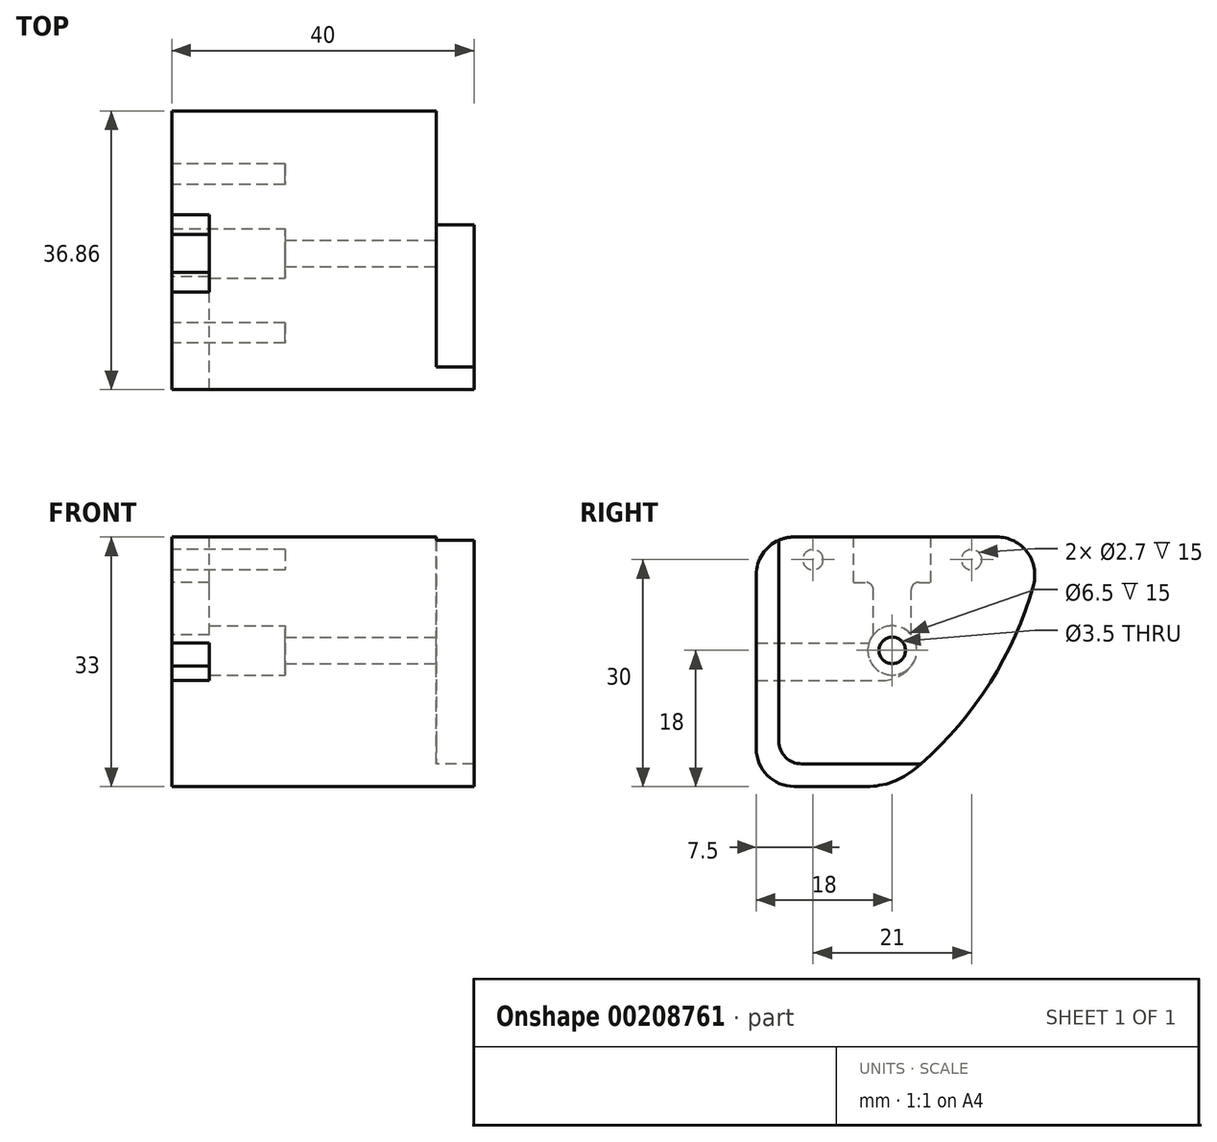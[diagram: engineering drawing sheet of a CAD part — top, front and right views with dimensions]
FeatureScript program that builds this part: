
annotation { "Feature Type Name" : "Feature", "Feature Type Description" : "" }
export const myFeature = defineFeature(function(context is Context, id is Id, definition is map)
    precondition{}
    {
        {
            var Q0;
            Q0=qCreatedBy(makeId("Right.planeOp"),FACE);
            var sketch = newSketch(context, id + "F0", { "sketchPlane" : qUnion([Q0])});
            skLineSegment(sketch, "E0", {"start": v(0, 0) * mm, "end": v(-15, 0) * mm, "construction": true});
            skLineSegment(sketch, "E1", {"start": v(-15, 0) * mm, "end": v(-15, -15) * mm});
            skLineSegment(sketch, "E2", {"start": v(-15, -15) * mm, "end": v(0, -15) * mm});
            skCircle(sketch, "E3", {"center": v(0, 0) * mm, "radius": 1.75 * mm});
            skLineSegment(sketch, "E4", {"start": v(-18, 0) * mm, "end": v(-18, -18) * mm});
            skLineSegment(sketch, "E5", {"start": v(-18, -18) * mm, "end": v(0, -18) * mm});
            skLineSegment(sketch, "E6", {"start": v(0, -18) * mm, "end": v(20, -18) * mm});
            skLineSegment(sketch, "E7", {"start": v(-18, 0) * mm, "end": v(-18, 15) * mm});
            skLineSegment(sketch, "E8", {"start": v(-18, 15) * mm, "end": v(20, 15) * mm});
            skLineSegment(sketch, "E9", {"start": v(20, 15) * mm, "end": v(20, -18) * mm});
            skLineSegment(sketch, "E10", {"start": v(0, -15) * mm, "end": v(0, -18) * mm});
            skLineSegment(sketch, "E11", {"start": v(-15, 0) * mm, "end": v(-15, 15) * mm});
            skLineSegment(sketch, "E12", {"start": v(-15, 0) * mm, "end": v(-18, 0) * mm, "construction": true});
            skArc(sketch, "E13", {"start": v(0, -18) * mm, "mid": v(13.4, -3.56) * mm, "end": v(20, 15) * mm});
            skLineSegment(sketch, "E14", {"start": v(0, -15) * mm, "end": v(3.79, -15) * mm});
            skSolve(sketch);
        }
        {
            var Q0;
            Q0=makeQuery(id+"F0.imprint","IMPRINT",FACE,{"disambiguationData":[TD([[makeQuery(id+"F0.imprint","IMPRINT",EDGE,{"derivedFrom":sQuery(id+"F0.wireOp",EDGE,"E1")}),-1.0]])]});
            var Q1;
            {var subQ0=sQuery(id+"F0.wireOp",EDGE,"E10");Q1=makeQuery(id+"F0.imprint","IMPRINT",FACE,{"disambiguationData":[TD([[makeQuery(id+"F0.imprint","IMPRINT",EDGE,{"derivedFrom":subQ0}),1.0]])]});}
            extrude(context, id + "F1", {"entities" : qUnion([Q0, Q1]), "depth" : 5 * mm});
        }
        {
            var Q0;
            Q0=makeQuery(id+"F0.imprint","IMPRINT",FACE,{"disambiguationData":[TD([[makeQuery(id+"F0.imprint","IMPRINT",EDGE,{"derivedFrom":sQuery(id+"F0.wireOp",EDGE,"E1")}),1.0]])]});
            var Q1;
            Q1=makeQuery(id+"F0.imprint","IMPRINT",FACE,{"disambiguationData":[TD([[makeQuery(id+"F0.imprint","IMPRINT",EDGE,{"derivedFrom":sQuery(id+"F0.wireOp",EDGE,"E1")}),-1.0]])]});
            var Q2;
            {var subQ0=sQuery(id+"F0.wireOp",EDGE,"E10");Q2=makeQuery(id+"F0.imprint","IMPRINT",FACE,{"disambiguationData":[TD([[makeQuery(id+"F0.imprint","IMPRINT",EDGE,{"derivedFrom":subQ0}),1.0]])]});}
            extrude(context, id + "F2", {"entities" : qUnion([Q0, Q1, Q2]), "operationType" : NewBodyOperationType.ADD, "oppositeDirection" : true, "depth" : 20 * mm});
        }
        {
            var Q0;
            Q0=makeQuery(id+"F2.opExtrude","CAP_FACE",FACE,{"disambiguationData":[OSD([sQuery(id+"F0.wireOp",EDGE,"E3"),sQuery(id+"F0.wireOp",EDGE,"E4"),sQuery(id+"F0.wireOp",EDGE,"E5"),sQuery(id+"F0.wireOp",EDGE,"E6"),sQuery(id+"F0.wireOp",EDGE,"E7"),sQuery(id+"F0.wireOp",EDGE,"E8"),sQuery(id+"F0.wireOp",EDGE,"E9")])],"isStart":false});
            var sketch = newSketch(context, id + "F3", { "sketchPlane" : qUnion([Q0])});
            skCircle(sketch, "E15", {"center": v(0, 0) * mm, "radius": 3.25 * mm});
            skSolve(sketch);
        }
        {
            var Q0;
            Q0=makeQuery(id+"F3.imprint","IMPRINT",FACE,{"disambiguationData":[TD([[makeQuery(id+"F3.imprint","IMPRINT",EDGE,{"derivedFrom":sQuery(id+"F3.wireOp",EDGE,"E15")}),-1.0]])]});
            extrude(context, id + "F4", {"entities" : qUnion([Q0]), "operationType" : NewBodyOperationType.ADD, "depth" : 15 * mm});
        }
        {
            var Q0;
            Q0=makeQuery(id+"F4.opExtrude","CAP_FACE",FACE,{"disambiguationData":[OSD([sQuery(id+"F0.wireOp",EDGE,"E4"),sQuery(id+"F0.wireOp",EDGE,"E5"),sQuery(id+"F0.wireOp",EDGE,"E6"),sQuery(id+"F0.wireOp",EDGE,"E7"),sQuery(id+"F0.wireOp",EDGE,"E8"),sQuery(id+"F0.wireOp",EDGE,"E9"),sQuery(id+"F3.wireOp",EDGE,"E15")])],"isStart":false});
            var sketch = newSketch(context, id + "F5", { "sketchPlane" : qUnion([Q0])});
            skLineSegment(sketch, "E16", {"start": v(0, 0) * mm, "end": v(0, 12) * mm, "construction": true});
            skLineSegment(sketch, "E17", {"start": v(0, 12) * mm, "end": v(-10.5, 12) * mm, "construction": true});
            skLineSegment(sketch, "E18", {"start": v(0, 12) * mm, "end": v(10.5, 12) * mm, "construction": true});
            skCircle(sketch, "E19", {"center": v(-10.5, 12) * mm, "radius": 1.35 * mm});
            skCircle(sketch, "E20", {"center": v(10.5, 12) * mm, "radius": 1.35 * mm});
            skLineSegment(sketch, "E21.bottom", {"start": v(5.1, 9) * mm, "end": v(-5.1, 9) * mm});
            skLineSegment(sketch, "E21.top", {"start": v(5.1, 15) * mm, "end": v(-5.1, 15) * mm});
            skLineSegment(sketch, "E21.left", {"start": v(5.1, 9) * mm, "end": v(5.1, 15) * mm});
            skLineSegment(sketch, "E21.right", {"start": v(-5.1, 9) * mm, "end": v(-5.1, 15) * mm});
            skPoint(sketch, "E21.middle", {"position": v(0, 12) * mm});
            skLineSegment(sketch, "E22", {"start": v(18, -1.5) * mm, "end": v(0, -1.5) * mm, "construction": true});
            skLineSegment(sketch, "E23.bottom", {"start": v(18, -4) * mm, "end": v(0, -4) * mm});
            skLineSegment(sketch, "E23.top", {"start": v(18, 1) * mm, "end": v(0, 1) * mm});
            skLineSegment(sketch, "E23.left", {"start": v(18, -4) * mm, "end": v(18, 1) * mm, "construction": true});
            skLineSegment(sketch, "E23.right", {"start": v(0, -4) * mm, "end": v(0, 1) * mm, "construction": true});
            skPoint(sketch, "E23.middle", {"position": v(9, -1.5) * mm});
            skLineSegment(sketch, "E24.bottom", {"start": v(2.5, -4) * mm, "end": v(-2.5, -4) * mm});
            skLineSegment(sketch, "E24.top", {"start": v(2.5, 16) * mm, "end": v(-2.5, 16) * mm});
            skLineSegment(sketch, "E24.left", {"start": v(2.5, -4) * mm, "end": v(2.5, 16) * mm});
            skLineSegment(sketch, "E24.right", {"start": v(-2.5, -4) * mm, "end": v(-2.5, 16) * mm});
            skPoint(sketch, "E24.middle", {"position": v(0, 6) * mm});
            skSolve(sketch);
        }
        {
            var Q0;
            Q0=makeQuery(id+"F5.imprint","IMPRINT",FACE,{"disambiguationData":[TD([[makeQuery(id+"F5.imprint","IMPRINT",EDGE,{"derivedFrom":sQuery(id+"F5.wireOp",EDGE,"E19")}),1.0]])]});
            var Q1;
            {var subQ0=sQuery(id+"F5.wireOp",EDGE,"E21.right");Q1=makeQuery(id+"F5.imprint","IMPRINT",FACE,{"disambiguationData":[TD([[makeQuery(id+"F5.imprint","IMPRINT",EDGE,{"derivedFrom":subQ0}),-1.0]])]});}
            var Q2;
            {var subQ0=sQuery(id+"F5.wireOp",EDGE,"E24.left");var subQ1=sQuery(id+"F5.wireOp",EDGE,"E21.bottom");var subQ2=makeQuery(id+"F5.imprint","INTERSECT",VERTEX,{"derivedFrom":[subQ1,subQ0]});Q2=makeQuery(id+"F5.imprint","IMPRINT",FACE,{"disambiguationData":[TD([[makeQuery(id+"F5.imprint","IMPRINT",EDGE,{"disambiguationData":[TD([[subQ2,-1.0]])],"derivedFrom":subQ1}),-1.0]])]});}
            var Q3;
            {var subQ0=sQuery(id+"F5.wireOp",EDGE,"E21.left");Q3=makeQuery(id+"F5.imprint","IMPRINT",FACE,{"disambiguationData":[TD([[makeQuery(id+"F5.imprint","IMPRINT",EDGE,{"derivedFrom":subQ0}),1.0]])]});}
            var Q4;
            {var subQ0=sQuery(id+"F5.wireOp",EDGE,"E24.left");var subQ1=sQuery(id+"F5.wireOp",EDGE,"E21.bottom");var subQ2=makeQuery(id+"F5.imprint","INTERSECT",VERTEX,{"derivedFrom":[subQ1,subQ0]});Q4=makeQuery(id+"F5.imprint","IMPRINT",FACE,{"disambiguationData":[TD([[makeQuery(id+"F5.imprint","IMPRINT",EDGE,{"disambiguationData":[TD([[subQ2,-1.0]])],"derivedFrom":subQ1}),1.0]])]});}
            var Q5;
            {var subQ0=sQuery(id+"F5.wireOp",EDGE,"E23.bottom");Q5=makeQuery(id+"F5.imprint","IMPRINT",FACE,{"disambiguationData":[TD([[makeQuery(id+"F5.imprint","IMPRINT",EDGE,{"derivedFrom":subQ0}),-1.0]])]});}
            var Q6;
            {var subQ1=sQuery(id+"F5.wireOp",EDGE,"E24.bottom");var subQ8=makeQuery(id+"F5.imprint","IMPRINT",VERTEX,{"derivedFrom":subQ1});Q6=makeQuery(id+"F5.imprint","IMPRINT",FACE,{"disambiguationData":[TD([[makeQuery(id+"F5.imprint","IMPRINT",EDGE,{"disambiguationData":[TD([[subQ8,-1.0]])],"derivedFrom":subQ1}),-1.0]])]});}
            var Q7;
            Q7=makeQuery(id+"F5.imprint","IMPRINT",FACE,{"disambiguationData":[TD([[makeQuery(id+"F5.imprint","IMPRINT",EDGE,{"derivedFrom":sQuery(id+"F5.wireOp",EDGE,"E20")}),1.0]])]});
            extrude(context, id + "F6", {"entities" : qUnion([Q0, Q1, Q2, Q3, Q4, Q5, Q6, Q7]), "operationType" : NewBodyOperationType.REMOVE, "oppositeDirection" : true, "depth" : 5 * mm});
        }
        {
            var Q0;
            Q0=makeQuery(id+"F6.boolean.opBoolean","COPY",FACE,{"derivedFrom":makeQuery(id+"F6.opExtrude","CAP_FACE",FACE,{"disambiguationData":[OSD([sQuery(id+"F5.wireOp",EDGE,"E19")])],"isStart":false})});
            var Q1;
            Q1=makeQuery(id+"F6.boolean.opBoolean","COPY",FACE,{"derivedFrom":makeQuery(id+"F6.opExtrude","CAP_FACE",FACE,{"disambiguationData":[OSD([sQuery(id+"F5.wireOp",EDGE,"E20")])],"isStart":false})});
            extrude(context, id + "F7", {"entities" : qUnion([Q0, Q1]), "operationType" : NewBodyOperationType.REMOVE, "oppositeDirection" : true, "depth" : 10 * mm});
        }
        {
            var Q0;
            Q0=makeQuery(id+"F1.opExtrude","SWEPT_EDGE",EDGE,{"disambiguationData":[OSD([sQuery(id+"F0.wireOp",EDGE,"E1"),sQuery(id+"F0.wireOp",EDGE,"E2")])]});
            fillet(context, id + "F8", {"entities" : qUnion([Q0]), "radius" : 3 * mm, "tangentPropagation" : true, "allowEdgeOverflow" : false});
        }
        {
            var Q0;
            {var subQ0=sQuery(id+"F0.wireOp",EDGE,"E5");var subQ1=sQuery(id+"F0.wireOp",EDGE,"E4");Q0=makeQuery(id+"F4.boolean.opBoolean","MERGE",EDGE,{"derivedFrom":[makeQuery(id+"F2.boolean.opBoolean","MERGE",EDGE,{"derivedFrom":[makeQuery(id+"F1.opExtrude","SWEPT_EDGE",EDGE,{"disambiguationData":[OSD([subQ1,subQ0])]}),makeQuery(id+"F2.opExtrude","SWEPT_EDGE",EDGE,{"disambiguationData":[OSD([subQ1,subQ0])]})]}),makeQuery(id+"F4.opExtrude","SWEPT_EDGE",EDGE,{"disambiguationData":[OSD([subQ1,subQ0,sQuery(id+"F0.wireOp",EDGE,"E6"),sQuery(id+"F0.wireOp",EDGE,"E7")])]})]});}
            fillet(context, id + "F9", {"entities" : qUnion([Q0]), "radius" : 5 * mm, "tangentPropagation" : true, "allowEdgeOverflow" : false});
        }
        {
            var Q0;
            Q0=makeQuery(id+"F6.boolean.opBoolean","COPY",EDGE,{"derivedFrom":makeQuery(id+"F6.opExtrude","SWEPT_EDGE",EDGE,{"disambiguationData":[OSD([sQuery(id+"F5.wireOp",EDGE,"E24.bottom"),sQuery(id+"F5.wireOp",EDGE,"E24.right")])]})});
            fillet(context, id + "F10", {"entities" : qUnion([Q0]), "radius" : 5 * mm, "tangentPropagation" : true, "allowEdgeOverflow" : false});
        }
        {
            var Q0;
            Q0=makeQuery(id+"F6.boolean.opBoolean","COPY",EDGE,{"derivedFrom":makeQuery(id+"F6.opExtrude","SWEPT_EDGE",EDGE,{"disambiguationData":[OSD([sQuery(id+"F5.wireOp",EDGE,"E21.bottom"),sQuery(id+"F5.wireOp",EDGE,"E24.right")])]})});
            var Q1;
            Q1=makeQuery(id+"F6.boolean.opBoolean","COPY",EDGE,{"derivedFrom":makeQuery(id+"F6.opExtrude","SWEPT_EDGE",EDGE,{"disambiguationData":[OSD([sQuery(id+"F5.wireOp",EDGE,"E21.bottom"),sQuery(id+"F5.wireOp",EDGE,"E24.left")])]})});
            fillet(context, id + "F11", {"entities" : qUnion([Q0, Q1]), "radius" : 1 * mm, "tangentPropagation" : true, "allowEdgeOverflow" : false});
        }
        {
            var Q0;
            {var subQ0=sQuery(id+"F0.wireOp",EDGE,"E13");var subQ1=sQuery(id+"F0.wireOp",EDGE,"E8");Q0=makeQuery(id+"F4.boolean.opBoolean","MERGE",EDGE,{"derivedFrom":[makeQuery(id+"F2.opExtrude","SWEPT_EDGE",EDGE,{"disambiguationData":[OSD([subQ1,sQuery(id+"F0.wireOp",EDGE,"E9"),subQ0])]}),makeQuery(id+"F4.opExtrude","SWEPT_EDGE",EDGE,{"disambiguationData":[OSD([subQ1,subQ0])]})]});}
            fillet(context, id + "F12", {"entities" : qUnion([Q0]), "radius" : 5 * mm, "tangentPropagation" : true, "allowEdgeOverflow" : false});
        }
        {
            var Q0;
            {var subQ0=sQuery(id+"F0.wireOp",EDGE,"E8");var subQ1=sQuery(id+"F0.wireOp",EDGE,"E7");Q0=makeQuery(id+"F4.boolean.opBoolean","MERGE",EDGE,{"derivedFrom":[makeQuery(id+"F2.boolean.opBoolean","MERGE",EDGE,{"derivedFrom":[makeQuery(id+"F1.opExtrude","SWEPT_EDGE",EDGE,{"disambiguationData":[OSD([subQ1,subQ0])]}),makeQuery(id+"F2.opExtrude","SWEPT_EDGE",EDGE,{"disambiguationData":[OSD([subQ1,subQ0])]})]}),makeQuery(id+"F4.opExtrude","SWEPT_EDGE",EDGE,{"disambiguationData":[OSD([sQuery(id+"F0.wireOp",EDGE,"E4"),subQ1,subQ0])]})]});}
            fillet(context, id + "F13", {"entities" : qUnion([Q0]), "radius" : 5 * mm, "tangentPropagation" : true, "allowEdgeOverflow" : false});
        }
        {
            var Q0;
            {var subQ0=sQuery(id+"F0.wireOp",EDGE,"E13");var subQ1=sQuery(id+"F0.wireOp",EDGE,"E5");Q0=makeQuery(id+"F4.boolean.opBoolean","MERGE",EDGE,{"derivedFrom":[makeQuery(id+"F2.opExtrude","SWEPT_EDGE",EDGE,{"disambiguationData":[OSD([subQ1,sQuery(id+"F0.wireOp",EDGE,"E6"),sQuery(id+"F0.wireOp",EDGE,"E10"),subQ0])]}),makeQuery(id+"F4.opExtrude","SWEPT_EDGE",EDGE,{"disambiguationData":[OSD([subQ1,subQ0])]})]});}
            fillet(context, id + "F14", {"entities" : qUnion([Q0]), "radius" : 10 * mm, "tangentPropagation" : true, "allowEdgeOverflow" : false});
        }
    });
